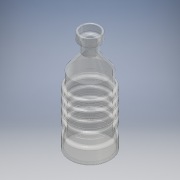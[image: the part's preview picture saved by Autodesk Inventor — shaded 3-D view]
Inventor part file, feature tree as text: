
AUTODESK INVENTOR PART (.ipt)
format: ipt  version: 2016 (Build 200138000, 138)  size: 542,720 bytes
history: native  units: mm
features: other x2, revolve x1, sketch x1
ambient origin geometry x8: Origin, YZ Plane, XZ Plane, XY Plane, X Axis, Y Axis, Z Axis, Center Point
bodies: Body1 (feature_tree)
feature tree (4):
  other  "Sólido1"
  revolve  "Revolución1"  [1 undecoded]
  other  "Desplazar cuerpo1"
  sketch  "Boceto1"  dims[d1=30.0mm d2=25.0mm d5=12.0mm d7=12.0mm d9=12.0mm d13=40.0mm d14=3.0mm d15=3.0mm d16=3.0mm d17=3.0mm d18=3.0mm d19=3.0mm d20=3.0mm d21=3.0mm d22=3.0mm d23=3.0mm d24=3.0mm d25=3.0mm d26=3.0mm d27=3.0mm d28=3.0mm d29=3.0mm d30=3.0mm d31=3.0mm d32=3.0mm d34=3.0mm d37=3.0mm d38=3.0mm d39=3.0mm d40=3.0mm d43=3.0mm d44=3.0mm d45=3.0mm d46=3.0mm d47=3.0mm d48=3.0mm d49=3.0mm d50=3.0mm d51=3.0mm d52=3.0mm d53=3.0mm d54=3.0mm d55=2.0mm d56=3.0mm d57=3.0mm d58=3.0mm d59=3.0mm d61=12.0mm d62=12.0mm d63=20.0mm d64=12.0mm d65=12.0mm d66=200.0mm d67=3.0mm d68=3.0mm d69=90.0deg d70=30.0mm d73=10.0mm d74=25.0mm d75=20.0mm d76=16.0mm d77=90.0deg]
note: 1 required parameter value undecoded (feature->parameter linkage not recoverable at this tier; creation-order binding heuristic only, values carry confidence <= 0.55)
